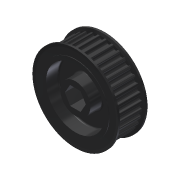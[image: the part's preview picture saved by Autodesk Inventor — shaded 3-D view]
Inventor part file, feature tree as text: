
AUTODESK INVENTOR PART (.ipt)
format: ipt  version: 2013 (Build 170138000, 138)  size: 830,976 bytes
history: native  units: in
note: dims shown in document units (in); Inventor stores cm internally (conversion verified against a paired STEP export)
features: mirror x1, other x1, imported_body x1
ambient origin geometry x8: Origin, YZ Plane, XZ Plane, XY Plane, X Axis, Y Axis, Z Axis, Center Point
feature tree (3):
  mirror  "Mirror1"
  other  "217-3232-STEP1"
  imported_body  "Base1"
